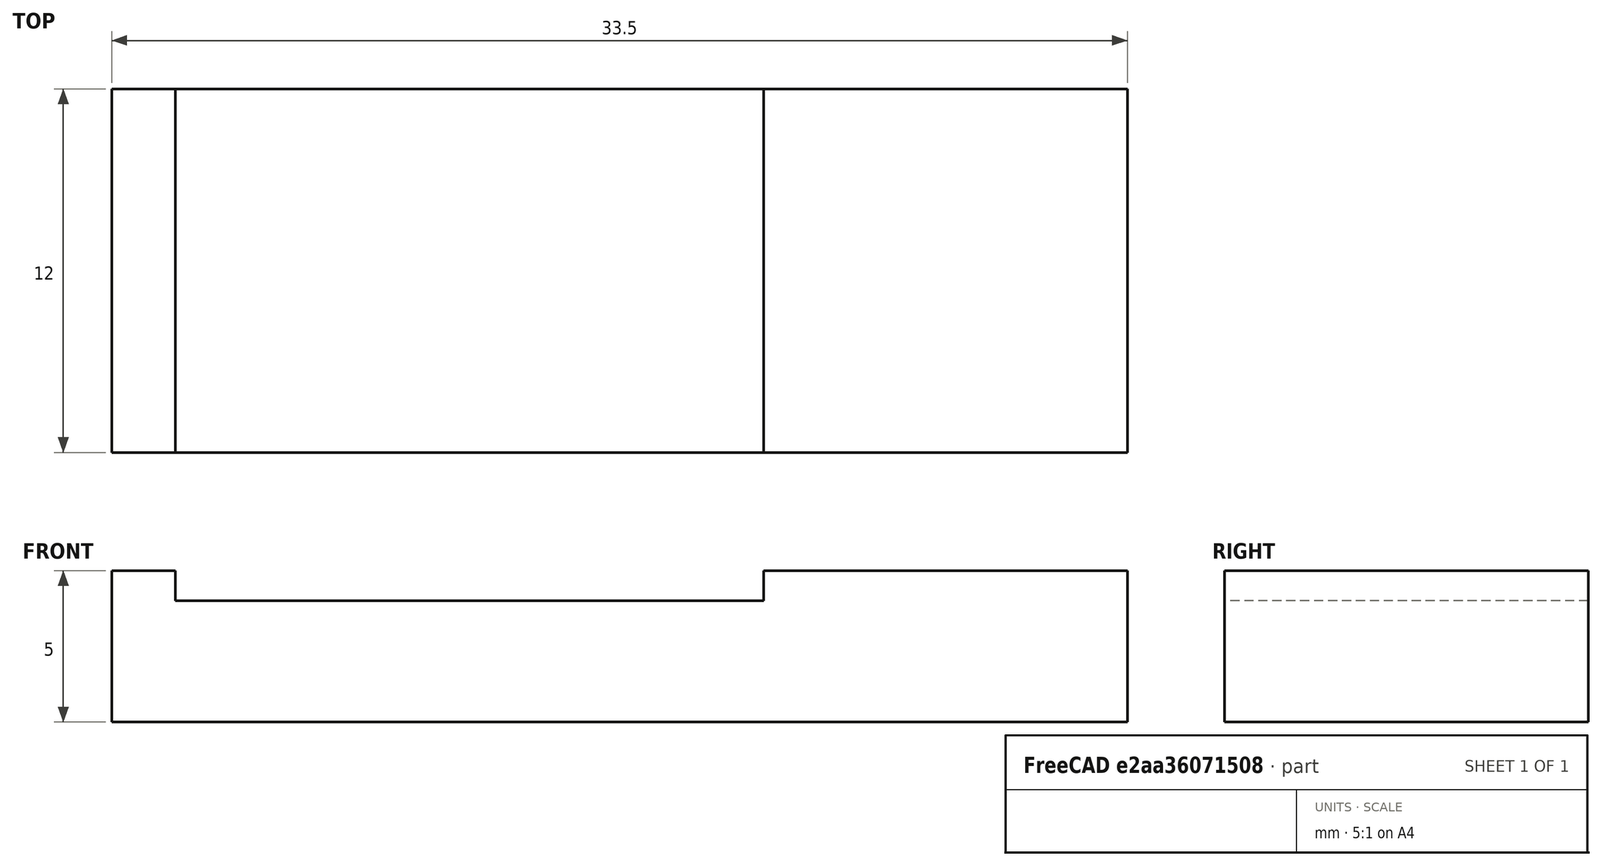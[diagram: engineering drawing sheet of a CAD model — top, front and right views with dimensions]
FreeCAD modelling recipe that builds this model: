
FCSTD DOCUMENT  (FreeCAD 0.20R29177 (Git))
Label: caleOled001
License: All rights reserved
LicenseURL: http://en.wikipedia.org/wiki/All_rights_reserved
objects: App::Link×1, Spreadsheet::Sheet×1, Sketcher::SketchObject×1, PartDesign::Pad×1, PartDesign::Body×1, App::Part×1
note: 4 computed .brp shape members not serialized (recipe doc carries the construction recipe); baked Part::Feature solids carry a one-line shape summary decoded from their .brp
EXTERNAL_REF file=modelsExterns/oled128x32_001.FCStd obj=Part

FEATURE [App::Link] Link  label="oled"
  LinkedObject = -> <external modelsExterns/oled128x32_001.FCStd>#Part
FEATURE [Spreadsheet::Sheet] Spreadsheet  label="caleSp"
  cells = A2=larg; B2(larg)=12; A3=long; B3(long)=33.5; A4=haut; B4(haut)=5; A5=degagementL1; B5(degagementL1)=31.4; A6=degagementL2; B6(degagementL2)=12; A7=degagementH; B7(degagementH)=1
FEATURE [Sketcher::SketchObject] Sketch
  FullyConstrained = true
  MapMode = 5
  Placement = pos=(0,0,0) rot=(1,0,0;1.5708rad)
  Support = -> [XZ_Plane001]
  expr: Constraints[17] = <<caleSp>>.degagementL2
  expr: Constraints[18] = <<caleSp>>.degagementL1
  expr: Constraints[20] = <<caleSp>>.long
  expr: Constraints[21] = <<caleSp>>.degagementH
  expr: Constraints[22] = <<caleSp>>.haut
  sketch-geometry (8):
    g0: LineSegment StartX=-14.3 StartY=-5 StartZ=0 EndX=19.2 EndY=-5 EndZ=0
    g1: LineSegment StartX=19.2 StartY=-5 StartZ=0 EndX=19.2 EndY=0 EndZ=0
    g2: LineSegment StartX=19.2 StartY=0 StartZ=0 EndX=7.2 EndY=0 EndZ=0
    g3: LineSegment StartX=7.2 StartY=0 StartZ=0 EndX=7.2 EndY=-1 EndZ=0
    g4: LineSegment StartX=7.2 StartY=-1 StartZ=0 EndX=-12.2 EndY=-1 EndZ=0
    g5: LineSegment StartX=-12.2 StartY=-1 StartZ=0 EndX=-12.2 EndY=0 EndZ=0
    g6: LineSegment StartX=-12.2 StartY=0 StartZ=0 EndX=-14.3 EndY=0 EndZ=0
    g7: LineSegment StartX=-14.3 StartY=0 StartZ=0 EndX=-14.3 EndY=-5 EndZ=0
  constraints (24):
    c: Horizontal(g0)
    c: Coincident(g0,g1)
    c: PointOnObject(g1,g-1)
    c: Vertical(g1)
    c: Coincident(g1,g2)
    c: PointOnObject(g2,g-1)
    c: Coincident(g2,g3)
    c: Vertical(g3)
    c: Coincident(g3,g4)
    c: Horizontal(g4)
    c: Coincident(g4,g5)
    c: PointOnObject(g5,g-1)
    c: Coincident(g5,g6)
    c: PointOnObject(g6,g-1)
    c: Coincident(g6,g7)
    c: Coincident(g7,g0)
    c: Vertical(g7)
    c: DistanceX(g2,g1) = 12
    c: DistanceX(g5,g1) = 31.4
    c: Vertical(g5)
    c: DistanceX(g6,g1) = 33.5
    c: DistanceY(g3,g2) = 1
    c: DistanceY(g0,g1) = 5
    c: DistanceX(g-1,g1) = 19.2
FEATURE [PartDesign::Pad] Pad
  Direction = (0,-1,2e-16)
  Length = 12
  Length2 = 10
  Midplane = true
  Placement = pos=(0,0,0) rot=(1,0,0;1.5708rad)
  Profile = -> Sketch
  ReferenceAxis = -> Sketch [N_Axis]
  Type = 0
  expr: Length = <<caleSp>>.larg
FEATURE [PartDesign::Body] Body  label="caleBdy"
  Group = -> [Sketch,Pad]
  Origin = -> Origin001
  Tip = -> Pad
FEATURE [App::Part] Part  label="calePrt"
  Group = -> [Body,Spreadsheet]
  Origin = -> Origin
